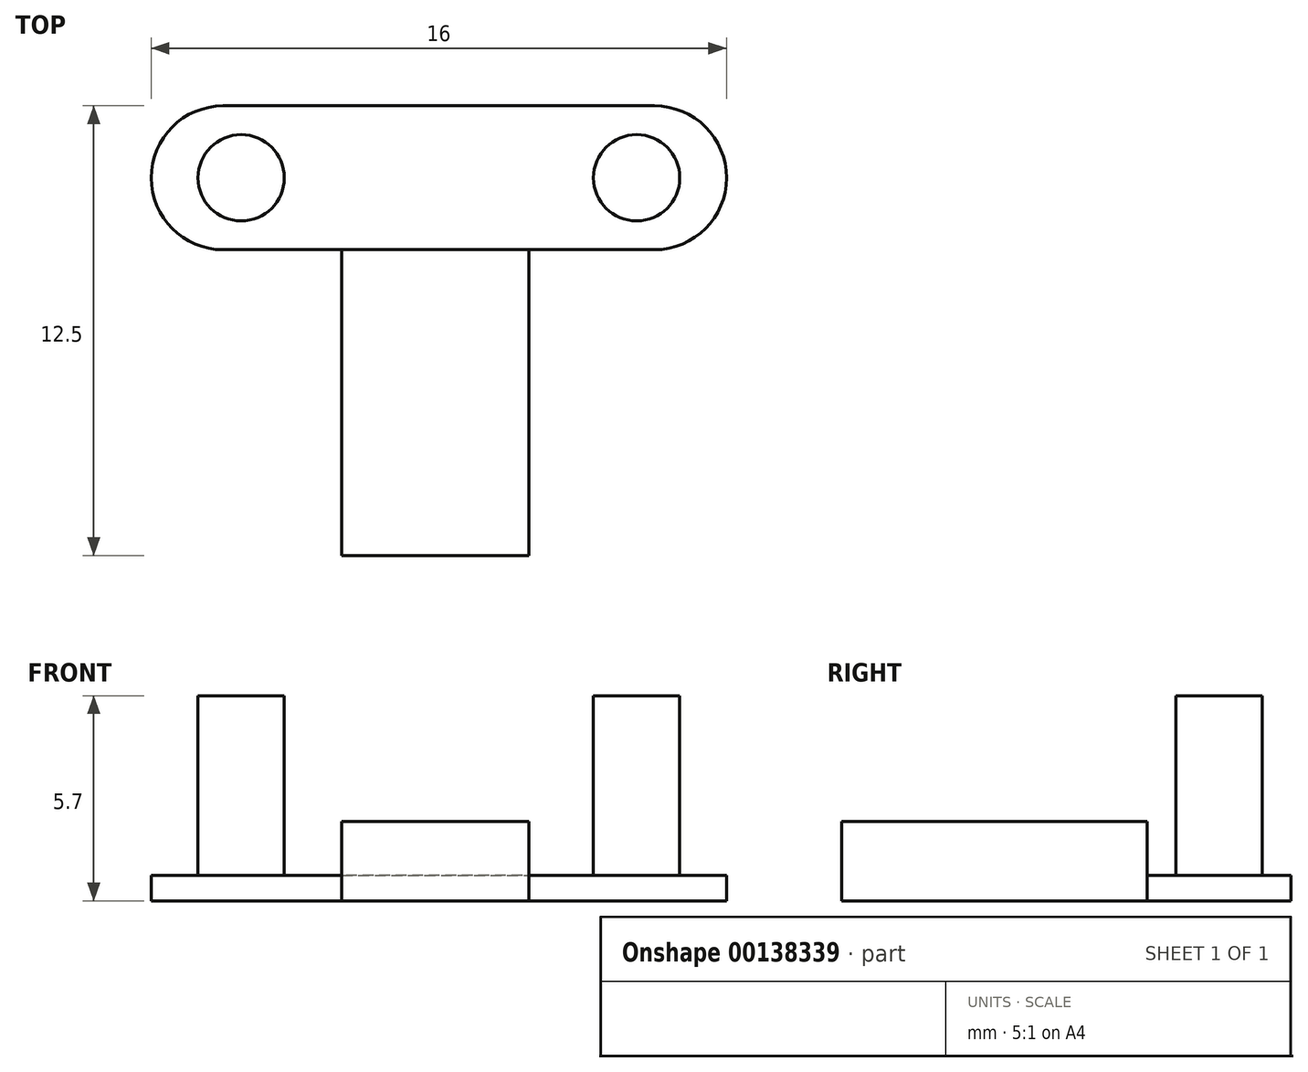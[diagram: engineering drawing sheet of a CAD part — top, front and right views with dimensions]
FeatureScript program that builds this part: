
annotation { "Feature Type Name" : "Feature", "Feature Type Description" : "" }
export const myFeature = defineFeature(function(context is Context, id is Id, definition is map)
    precondition{}
    {
        {
            var Q0;
            Q0=qCreatedBy(makeId("Front.planeOp"),FACE);
            var sketch = newSketch(context, id + "F0", { "sketchPlane" : qUnion([Q0])});
            skLineSegment(sketch, "E0.bottom", {"start": v(0, 0) * mm, "end": v(-5.2, 0) * mm});
            skLineSegment(sketch, "E0.top", {"start": v(0, 2.2) * mm, "end": v(-5.2, 2.2) * mm});
            skLineSegment(sketch, "E0.left", {"start": v(0, 0) * mm, "end": v(0, 2.2) * mm});
            skLineSegment(sketch, "E0.right", {"start": v(-5.2, 0) * mm, "end": v(-5.2, 2.2) * mm});
            skSolve(sketch);
        }
        {
            var Q0;
            Q0=makeQuery(id+"F0.imprint","IMPRINT",FACE,{"disambiguationData":[TD([[makeQuery(id+"F0.imprint","IMPRINT",EDGE,{"derivedFrom":sQuery(id+"F0.wireOp",EDGE,"E0.bottom")}),-1.0]])]});
            extrude(context, id + "F1", {"entities" : qUnion([Q0]), "oppositeDirection" : true, "depth" : 12.5 * mm});
        }
        {
            var Q0;
            Q0=makeQuery(id+"F1.opExtrude","SWEPT_FACE",FACE,{"disambiguationData":[OSD([sQuery(id+"F0.wireOp",EDGE,"E0.top")])]});
            var sketch = newSketch(context, id + "F2", { "sketchPlane" : qUnion([Q0])});
            skLineSegment(sketch, "E1.bottom", {"start": v(-5.2, 12.5) * mm, "end": v(0, 12.5) * mm});
            skLineSegment(sketch, "E1.top", {"start": v(-5.2, 8.5) * mm, "end": v(0, 8.5) * mm});
            skLineSegment(sketch, "E1.left", {"start": v(-5.2, 12.5) * mm, "end": v(-5.2, 8.5) * mm});
            skLineSegment(sketch, "E1.right", {"start": v(0, 12.5) * mm, "end": v(0, 8.5) * mm});
            skSolve(sketch);
        }
        {
            var Q0;
            Q0=makeQuery(id+"F2.imprint","IMPRINT",FACE,{"disambiguationData":[TD([[makeQuery(id+"F2.imprint","IMPRINT",EDGE,{"derivedFrom":sQuery(id+"F2.wireOp",EDGE,"E1.bottom")}),1.0]])]});
            extrude(context, id + "F3", {"entities" : qUnion([Q0]), "operationType" : NewBodyOperationType.ADD, "depth" : 3.5 * mm});
        }
        {
            var Q0;
            Q0=makeQuery(id+"F3.boolean.opBoolean","MERGE",FACE,{"derivedFrom":[makeQuery(id+"F1.opExtrude","SWEPT_FACE",FACE,{"disambiguationData":[OSD([sQuery(id+"F0.wireOp",EDGE,"E0.left")])]}),makeQuery(id+"F3.opExtrude","SWEPT_FACE",FACE,{"disambiguationData":[OSD([sQuery(id+"F2.wireOp",EDGE,"E1.right")])]})]});
            var sketch = newSketch(context, id + "F4", { "sketchPlane" : qUnion([Q0])});
            skLineSegment(sketch, "E2.bottom", {"start": v(12.5, 5.7) * mm, "end": v(8.5, 5.7) * mm});
            skLineSegment(sketch, "E2.top", {"start": v(12.5, 0) * mm, "end": v(8.5, 0) * mm});
            skLineSegment(sketch, "E2.left", {"start": v(12.5, 5.7) * mm, "end": v(12.5, 0) * mm});
            skLineSegment(sketch, "E2.right", {"start": v(8.5, 5.7) * mm, "end": v(8.5, 0) * mm});
            skSolve(sketch);
        }
        {
            var Q0;
            {var subQ4=sQuery(id+"F4.wireOp",EDGE,"E2.bottom");Q0=makeQuery(id+"F4.imprint","IMPRINT",FACE,{"disambiguationData":[TD([[makeQuery(id+"F4.imprint","IMPRINT",EDGE,{"derivedFrom":subQ4}),1.0]])]});}
            extrude(context, id + "F5", {"entities" : qUnion([Q0]), "operationType" : NewBodyOperationType.ADD, "oppositeDirection" : true, "depth" : 10.5 * mm, "hasSecondDirection" : true, "secondDirectionOppositeDirection" : false, "secondDirectionDepth" : 5.5 * mm});
        }
        {
            var Q0;
            Q0=makeQuery(id+"F5.boolean.opBoolean","MERGE",FACE,{"derivedFrom":[makeQuery(id+"F3.opExtrude","CAP_FACE",FACE,{"disambiguationData":[OSD([sQuery(id+"F2.wireOp",EDGE,"E1.bottom"),sQuery(id+"F2.wireOp",EDGE,"E1.top"),sQuery(id+"F2.wireOp",EDGE,"E1.left"),sQuery(id+"F2.wireOp",EDGE,"E1.right")])],"isStart":false}),makeQuery(id+"F5.opExtrude","SWEPT_FACE",FACE,{"disambiguationData":[OSD([sQuery(id+"F4.wireOp",EDGE,"E2.bottom")])]})]});
            var sketch = newSketch(context, id + "F6", { "sketchPlane" : qUnion([Q0])});
            skLineSegment(sketch, "E3", {"start": v(-10.5, 10.5) * mm, "end": v(5.5, 10.5) * mm});
            skLineSegment(sketch, "E4", {"start": v(-10.5, 10.5) * mm, "end": v(-8, 10.5) * mm});
            skLineSegment(sketch, "E5", {"start": v(5.5, 10.5) * mm, "end": v(3, 10.5) * mm});
            skCircle(sketch, "E6", {"center": v(-8, 10.5) * mm, "radius": 1.2 * mm});
            skCircle(sketch, "E7", {"center": v(3, 10.5) * mm, "radius": 1.2 * mm});
            skSolve(sketch);
        }
        {
            var Q0;
            {var subQ0=sQuery(id+"F6.wireOp",EDGE,"E4");var subQ1=sQuery(id+"F6.wireOp",EDGE,"E3");var subQ2=makeQuery(id+"F6.imprint","INTERSECT",VERTEX,{"derivedFrom":[subQ1,subQ0]});Q0=makeQuery(id+"F6.imprint","IMPRINT",FACE,{"disambiguationData":[TD([[makeQuery(id+"F6.imprint","IMPRINT",EDGE,{"disambiguationData":[TD([[subQ2,-1.0]])],"derivedFrom":subQ1}),1.0]])]});}
            var Q1;
            {var subQ0=sQuery(id+"F6.wireOp",EDGE,"E4");var subQ1=sQuery(id+"F6.wireOp",EDGE,"E3");var subQ2=makeQuery(id+"F6.imprint","INTERSECT",VERTEX,{"derivedFrom":[subQ1,subQ0]});Q1=makeQuery(id+"F6.imprint","IMPRINT",FACE,{"disambiguationData":[TD([[makeQuery(id+"F6.imprint","IMPRINT",EDGE,{"disambiguationData":[TD([[subQ2,-1.0]])],"derivedFrom":subQ1}),-1.0]])]});}
            var Q2;
            {var subQ0=sQuery(id+"F6.wireOp",EDGE,"E5");var subQ1=sQuery(id+"F6.wireOp",EDGE,"E3");var subQ2=makeQuery(id+"F6.imprint","INTERSECT",VERTEX,{"derivedFrom":[subQ1,subQ0]});Q2=makeQuery(id+"F6.imprint","IMPRINT",FACE,{"disambiguationData":[TD([[makeQuery(id+"F6.imprint","IMPRINT",EDGE,{"disambiguationData":[TD([[subQ2,1.0]])],"derivedFrom":subQ1}),-1.0]])]});}
            var Q3;
            {var subQ0=sQuery(id+"F6.wireOp",EDGE,"E5");var subQ1=sQuery(id+"F6.wireOp",EDGE,"E3");var subQ2=makeQuery(id+"F6.imprint","INTERSECT",VERTEX,{"derivedFrom":[subQ1,subQ0]});Q3=makeQuery(id+"F6.imprint","IMPRINT",FACE,{"disambiguationData":[TD([[makeQuery(id+"F6.imprint","IMPRINT",EDGE,{"disambiguationData":[TD([[subQ2,1.0]])],"derivedFrom":subQ1}),1.0]])]});}
            extrude(context, id + "F7", {"entities" : qUnion([Q0, Q1, Q2, Q3]), "operationType" : NewBodyOperationType.REMOVE, "oppositeDirection" : true, "depth" : 5 * mm});
        }
        {
            var Q0;
            Q0=makeQuery(id+"F5.opExtrude","CAP_EDGE",EDGE,{"disambiguationData":[OSD([sQuery(id+"F4.wireOp",EDGE,"E2.right")])],"isStart":true});
            var Q1;
            Q1=makeQuery(id+"F5.opExtrude","CAP_EDGE",EDGE,{"disambiguationData":[OSD([sQuery(id+"F4.wireOp",EDGE,"E2.left")])],"isStart":true});
            var Q2;
            Q2=makeQuery(id+"F5.opExtrude","CAP_EDGE",EDGE,{"disambiguationData":[OSD([sQuery(id+"F4.wireOp",EDGE,"E2.left")])],"isStart":false});
            var Q3;
            Q3=makeQuery(id+"F5.opExtrude","CAP_EDGE",EDGE,{"disambiguationData":[OSD([sQuery(id+"F4.wireOp",EDGE,"E2.right")])],"isStart":false});
            fillet(context, id + "F8", {"entities" : qUnion([Q0, Q1, Q2, Q3]), "radius" : 2 * mm, "tangentPropagation" : true, "allowEdgeOverflow" : false});
        }
    });
